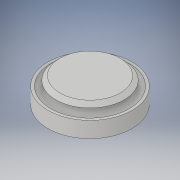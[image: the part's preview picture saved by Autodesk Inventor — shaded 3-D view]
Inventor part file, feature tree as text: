
AUTODESK INVENTOR PART (.ipt)
format: ipt  version: 2018 (Build 220112000, 112)  size: 158,208 bytes
history: native  units: in
note: dims shown in document units (in); Inventor stores cm internally (conversion verified against a paired STEP export)
features: sketch x3, revolve x1, chamfer x1, extrude x1, projected_geometry x1
ambient origin geometry x8: Origin, YZ Plane, XZ Plane, XY Plane, X Axis, Y Axis, Z Axis, Center Point
bodies: Solid1 (feature_tree)
feature tree (7):
  revolve  "Revolution1"  Angle=45.0deg
  chamfer  "Chamfer1"  Distance=0.25in
  sketch  "Sketch2"  dims[d6=0.0625in]
  extrude  "Extrusion2"  TaperAngle=90.0deg  [1 undecoded]
  sketch  "Sketch1"  dims[d0=0.125in d5=45.0deg]
  projected_geometry  "Projected Loop1"
  sketch  "Sketch4"  dims[d7=0.125in d8=0.25in d9=90.0deg d10=0.0625in d11=0.125in d12=45.0deg d13=0.5625in d14=0.115in d17=0.245in d18=0.3in d19=0.15in d20=2.3622in d22=360.0deg d24=1.0in d25=0.0in]
note: 1 required parameter value undecoded (feature->parameter linkage not recoverable at this tier; creation-order binding heuristic only, values carry confidence <= 0.55)
